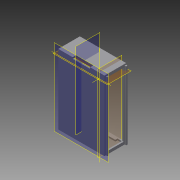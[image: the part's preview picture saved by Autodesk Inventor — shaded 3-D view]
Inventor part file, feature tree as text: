
AUTODESK INVENTOR PART (.ipt)
format: ipt  version: 2015 (Build 190159000, 159)  size: 257,536 bytes
history: native  units: mm
features: sketch x14, projected_geometry x11, extrude x9, sweep x1, plane x1, mirror x1
ambient origin geometry x8: Origin, YZ Plane, XZ Plane, XY Plane, X Axis, Y Axis, Z Axis, Center Point
bodies: Solid1 (feature_tree)
feature tree (37):
  sketch  "Sketch1"  dims[d0=2.5mm d1=20.0mm d3=49.0mm d4=20.0mm d6=58.0mm]
  extrude  "Extrusion1"  Depth=20.0mm
  extrude  "Extrusion2"  Depth=3.5mm
  sketch  "Sketch4"  dims[d14=3.5mm d15=2.0mm]
  sketch  "Sketch5"  dims[d16=2.0mm d17=0.0mm d18=2.0mm]
  sketch  "3D Sketch1"
  sweep  "Sweep2"
  extrude  "Extrusion3"  Depth=2.0mm
  extrude  "Extrusion5"  Depth=2.0mm
  extrude  "Extrusion6"  TaperAngle=0.0deg  [1 undecoded]
  sketch  "Sketch12"  dims[d41=5.0mm d42=2.0mm d43=0.0mm]
  sketch  "Sketch13"  dims[d44=5.0mm d45=5.0mm]
  extrude  "Extrusion10"  Depth=2.0mm TaperAngle=0.0deg
  extrude  "Extrusion11"  Depth=20.0mm
  extrude  "Extrusion12"  Depth=2.0mm TaperAngle=0.0deg
  plane  "Work Plane1"
  mirror  "Mirror1"
  extrude  "Extrusion13"  Depth=5.0mm
  sketch  "Sketch2"  dims[d9=10.0mm d10=0.0mm d11=3.5mm]
  sketch  "Sketch3"  dims[d12=27.0mm d13=3.5mm]
  projected_geometry  "Projected Loop1"
  projected_geometry  "Projected Loop2"
  projected_geometry  "Projected Loop3"
  projected_geometry  "Projected Loop4"
  sketch  "3D Sketch2"
  sketch  "Sketch6"  dims[d19=30.0mm d23=0.0mm d24=0.0mm]
  sketch  "Sketch8"  dims[d25=5.0mm d26=2.0mm d27=0.0mm]
  sketch  "Sketch9"  dims[d39=20.0mm d40=20.0mm]
  projected_geometry  "Projected Loop5"
  projected_geometry  "Projected Loop6"
  projected_geometry  "Projected Loop7"
  projected_geometry  "Projected Loop8"
  projected_geometry  "Projected Loop11"
  projected_geometry  "Projected Loop12"
  projected_geometry  "Projected Loop13"
  sketch  "Sketch14"  dims[d46=5.0mm]
  sketch  "Sketch15"  dims[d47=5.0mm d48=4.0mm d49=0.0mm d67=2.0mm d68=2.0mm d69=3.5mm d70=2.0mm d72=8.0mm d73=2.0mm d74=10.0mm d75=0.0mm d76=10.0mm d77=0.0mm d78=2.0mm d79=2.0mm d80=2.0mm d81=2.0mm d82=0.0mm d83=0.0mm d84=0.0mm d85=24.0mm d86=94.5mm d87=0.0mm d88=2.0mm d89=0.0mm]
note: 1 required parameter value undecoded (feature->parameter linkage not recoverable at this tier; creation-order binding heuristic only, values carry confidence <= 0.55)
